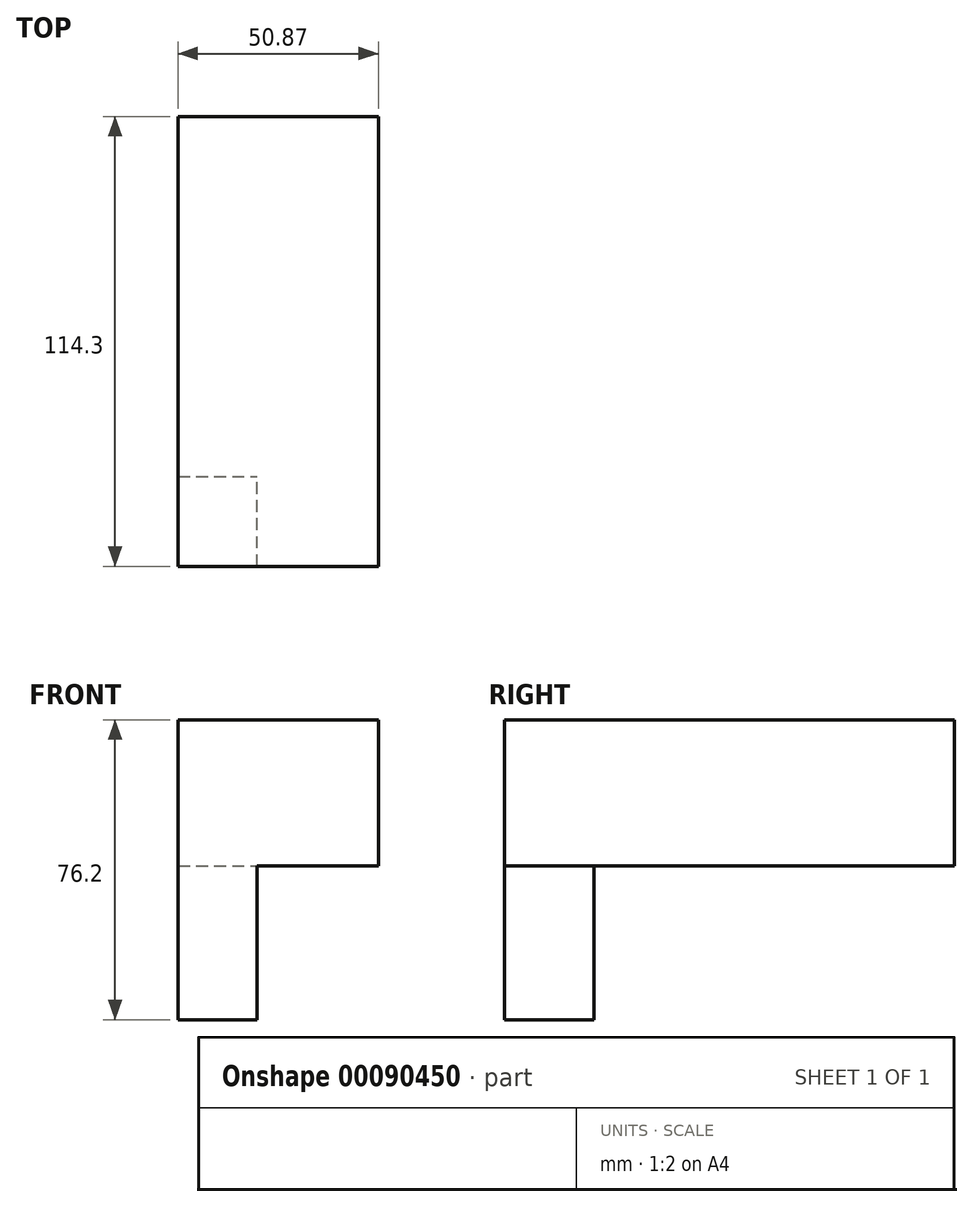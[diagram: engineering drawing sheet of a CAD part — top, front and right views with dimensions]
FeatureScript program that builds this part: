
annotation { "Feature Type Name" : "Feature", "Feature Type Description" : "" }
export const myFeature = defineFeature(function(context is Context, id is Id, definition is map)
    precondition{}
    {
        {
            var Q0;
            Q0=qCreatedBy(makeId("Front.planeOp"),FACE);
            var sketch = newSketch(context, id + "F0", { "sketchPlane" : qUnion([Q0])});
            skLineSegment(sketch, "E0.bottom", {"start": v(0, 0) * mm, "end": v(50.87, 0) * mm});
            skLineSegment(sketch, "E0.top", {"start": v(0, 37.1) * mm, "end": v(50.87, 37.1) * mm});
            skLineSegment(sketch, "E0.left", {"start": v(0, 0) * mm, "end": v(0, 37.1) * mm});
            skLineSegment(sketch, "E0.right", {"start": v(50.87, 0) * mm, "end": v(50.87, 37.1) * mm});
            skSolve(sketch);
        }
        {
            var Q0;
            Q0=makeQuery(id+"F0.imprint","IMPRINT",FACE,{"disambiguationData":[TD([[makeQuery(id+"F0.imprint","IMPRINT",EDGE,{"derivedFrom":sQuery(id+"F0.wireOp",EDGE,"E0.bottom")}),1.0]])]});
            extrude(context, id + "F1", {"entities" : qUnion([Q0]), "depth" : 114.3 * mm});
        }
        {
            var Q0;
            Q0=makeQuery(id+"F1.opExtrude","SWEPT_FACE",FACE,{"disambiguationData":[OSD([sQuery(id+"F0.wireOp",EDGE,"E0.top")])]});
            var sketch = newSketch(context, id + "F2", { "sketchPlane" : qUnion([Q0])});
            skLineSegment(sketch, "E1.bottom", {"start": v(0, -114.3) * mm, "end": v(20.1, -114.3) * mm});
            skLineSegment(sketch, "E1.top", {"start": v(0, -91.45) * mm, "end": v(20.1, -91.45) * mm});
            skLineSegment(sketch, "E1.left", {"start": v(0, -114.3) * mm, "end": v(0, -91.45) * mm});
            skLineSegment(sketch, "E1.right", {"start": v(20.1, -114.3) * mm, "end": v(20.1, -91.45) * mm});
            skSolve(sketch);
        }
        {
            var Q0;
            Q0=makeQuery(id+"F2.imprint","IMPRINT",FACE,{"disambiguationData":[TD([[makeQuery(id+"F2.imprint","IMPRINT",EDGE,{"derivedFrom":sQuery(id+"F2.wireOp",EDGE,"E1.bottom")}),1.0]])]});
            extrude(context, id + "F3", {"entities" : qUnion([Q0]), "operationType" : NewBodyOperationType.ADD, "oppositeDirection" : true, "depth" : 76.2 * mm});
        }
        {
            var Q0;
            Q0=makeQuery(id+"F3.boolean.opBoolean","MERGE",FACE,{"derivedFrom":[makeQuery(id+"F1.opExtrude","CAP_FACE",FACE,{"disambiguationData":[OSD([sQuery(id+"F0.wireOp",EDGE,"E0.bottom"),sQuery(id+"F0.wireOp",EDGE,"E0.top"),sQuery(id+"F0.wireOp",EDGE,"E0.left"),sQuery(id+"F0.wireOp",EDGE,"E0.right")])],"isStart":false}),makeQuery(id+"F3.opExtrude","SWEPT_FACE",FACE,{"disambiguationData":[OSD([sQuery(id+"F2.wireOp",EDGE,"E1.bottom")])]})]});
            var sketch = newSketch(context, id + "F4", { "sketchPlane" : qUnion([Q0])});
            skLineSegment(sketch, "E2", {"start": v(50.87, 37.1) * mm, "end": v(33.12, 37.1) * mm});
            skLineSegment(sketch, "E3", {"start": v(33.12, 37.1) * mm, "end": v(33.12, 14.27) * mm});
            skLineSegment(sketch, "E4", {"start": v(33.12, 14.27) * mm, "end": v(20.3, 14.27) * mm});
            skLineSegment(sketch, "E5", {"start": v(20.3, 14.27) * mm, "end": v(20.3, 37.1) * mm});
            skLineSegment(sketch, "E6", {"start": v(20.3, 37.1) * mm, "end": v(33.12, 37.1) * mm});
            skSolve(sketch);
        }
        {
            var Q0;
            Q0=makeQuery(id+"F4.imprint","IMPRINT",FACE,{"disambiguationData":[TD([[makeQuery(id+"F4.imprint","IMPRINT",EDGE,{"derivedFrom":sQuery(id+"F4.wireOp",EDGE,"E3")}),-1.0]])]});
            var sketch = newSketch(context, id + "F5", { "sketchPlane" : qUnion([Q0])});
            skSolve(sketch);
        }
        {
            var Q0;
            Q0 = qSketchRegion(id + "F5", true);
            var Q1;
            Q1=makeQuery(id+"F4.imprint","IMPRINT",FACE,{"disambiguationData":[TD([[makeQuery(id+"F4.imprint","IMPRINT",EDGE,{"derivedFrom":sQuery(id+"F4.wireOp",EDGE,"E3")}),-1.0]])]});
            extrude(context, id + "F6", {"entities" : qUnion([Q0, Q1]), "operationType" : NewBodyOperationType.ADD, "oppositeDirection" : true, "depth" : 5.08 * mm});
        }
    });
